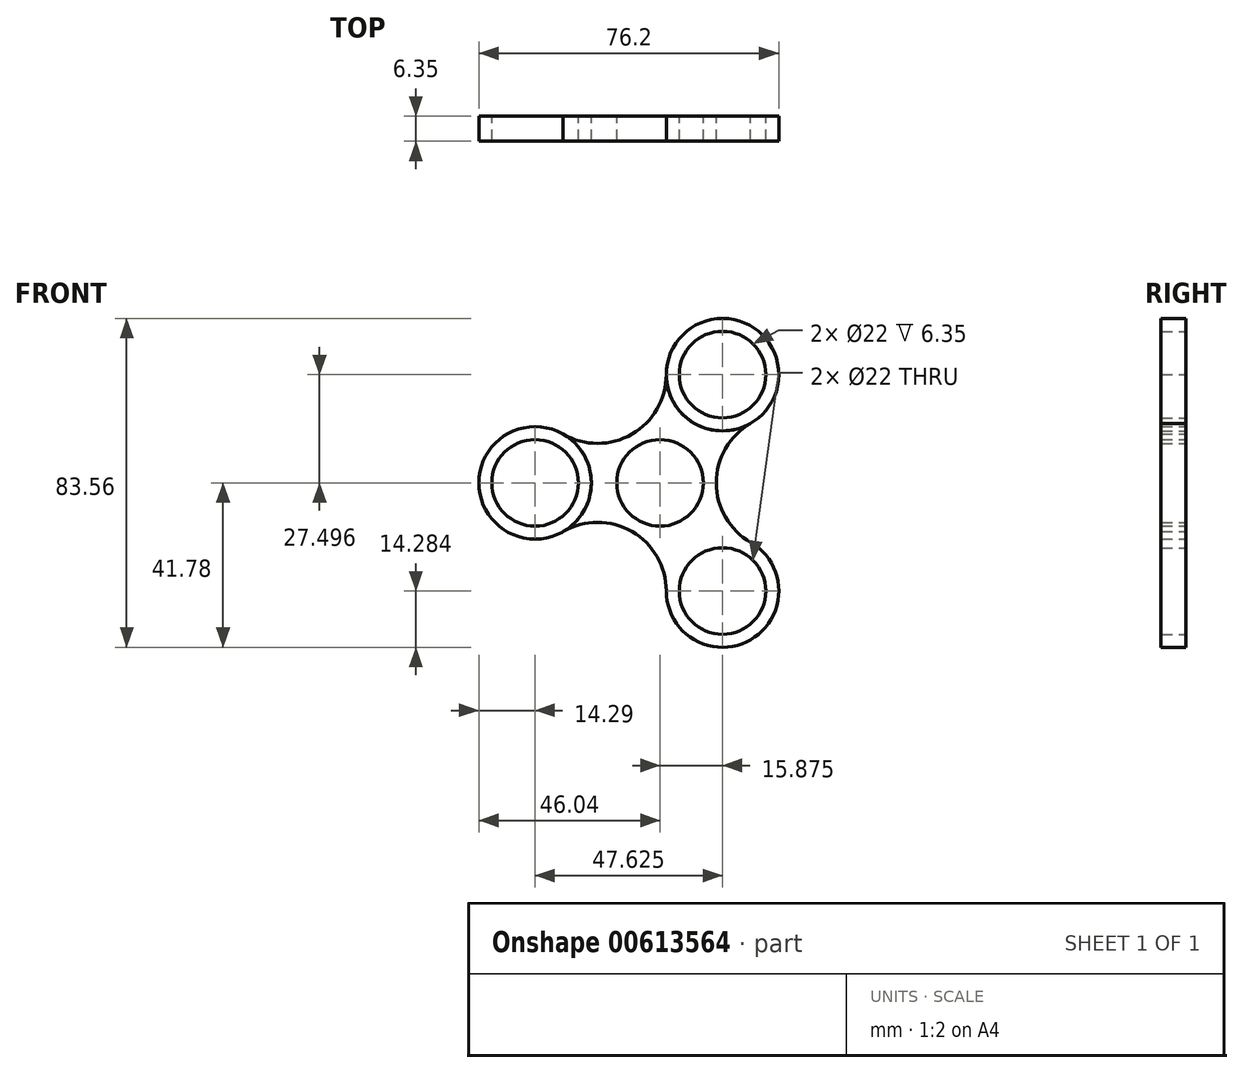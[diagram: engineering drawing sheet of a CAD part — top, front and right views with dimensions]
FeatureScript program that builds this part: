
annotation { "Feature Type Name" : "Feature", "Feature Type Description" : "" }
export const myFeature = defineFeature(function(context is Context, id is Id, definition is map)
    precondition{}
    {
        {
            var Q0;
            Q0=qCreatedBy(makeId("Front.planeOp"),FACE);
            var sketch = newSketch(context, id + "F0", { "sketchPlane" : qUnion([Q0])});
            skCircle(sketch, "E0", {"center": v(0, 0) * mm, "radius": 14.29 * mm});
            skCircle(sketch, "E1", {"center": v(0, 0) * mm, "radius": 11 * mm});
            skCircle(sketch, "E2", {"center": v(-31.75, 0) * mm, "radius": 14.29 * mm});
            skCircle(sketch, "E3", {"center": v(-31.75, 0) * mm, "radius": 11 * mm});
            skCircle(sketch, "E4.1.0", {"center": v(15.87, -27.5) * mm, "radius": 11 * mm});
            skCircle(sketch, "E4.1.1", {"center": v(15.87, -27.5) * mm, "radius": 14.29 * mm});
            skCircle(sketch, "E4.2.0", {"center": v(15.88, 27.5) * mm, "radius": 11 * mm});
            skCircle(sketch, "E4.2.1", {"center": v(15.88, 27.5) * mm, "radius": 14.29 * mm});
            skSolve(sketch);
        }
        {
            var Q0;
            Q0=makeQuery(id+"F0.imprint","IMPRINT",FACE,{"disambiguationData":[TD([[makeQuery(id+"F0.imprint","IMPRINT",EDGE,{"derivedFrom":sQuery(id+"F0.wireOp",EDGE,"E1")}),1.0]])]});
            var sketch = newSketch(context, id + "F1", { "sketchPlane" : qUnion([Q0])});
            skArc(sketch, "E5", {"start": v(1.59, -27.5) * mm, "mid": v(-7.14, -12.37) * mm, "end": v(-24.6, -12.37) * mm});
            skArc(sketch, "E6", {"start": v(23.02, 15.12) * mm, "mid": v(14.29, 0) * mm, "end": v(23.02, -15.12) * mm});
            skArc(sketch, "E7", {"start": v(-24.6, 12.37) * mm, "mid": v(-7.14, 12.37) * mm, "end": v(1.59, 27.5) * mm});
            skCircle(sketch, "E8", {"center": v(-31.75, 0) * mm, "radius": 14.29 * mm});
            skCircle(sketch, "E9", {"center": v(-31.75, 0) * mm, "radius": 11 * mm});
            skCircle(sketch, "E10", {"center": v(15.88, 27.5) * mm, "radius": 14.29 * mm});
            skCircle(sketch, "E11", {"center": v(15.88, 27.5) * mm, "radius": 11 * mm});
            skCircle(sketch, "E12", {"center": v(15.87, -27.5) * mm, "radius": 14.29 * mm});
            skCircle(sketch, "E13", {"center": v(15.87, -27.5) * mm, "radius": 11 * mm});
            skSolve(sketch);
        }
        {
            var Q0;
            {var subQ1=sQuery(id+"F1.wireOp",EDGE,"E5");Q0=makeQuery(id+"F1.imprint","IMPRINT",FACE,{"disambiguationData":[TD([[makeQuery(id+"F1.imprint","IMPRINT",EDGE,{"derivedFrom":subQ1}),-1.0]])]});}
            var Q1;
            Q1=makeQuery(id+"F0.imprint","IMPRINT",FACE,{"disambiguationData":[TD([[makeQuery(id+"F0.imprint","IMPRINT",EDGE,{"derivedFrom":sQuery(id+"F0.wireOp",EDGE,"E2")}),1.0]])]});
            var Q2;
            Q2=makeQuery(id+"F0.imprint","IMPRINT",FACE,{"disambiguationData":[TD([[makeQuery(id+"F0.imprint","IMPRINT",EDGE,{"derivedFrom":sQuery(id+"F0.wireOp",EDGE,"E4.2.0")}),-1.0]])]});
            var Q3;
            Q3=makeQuery(id+"F1.imprint","IMPRINT",FACE,{"disambiguationData":[TD([[makeQuery(id+"F1.imprint","IMPRINT",EDGE,{"derivedFrom":sQuery(id+"F1.wireOp",EDGE,"E13")}),-1.0]])]});
            extrude(context, id + "F2", {"entities" : qUnion([Q0, Q1, Q2, Q3]), "depth" : 6.35 * mm, "offsetDistance" : 25.4 * mm});
        }
    });
